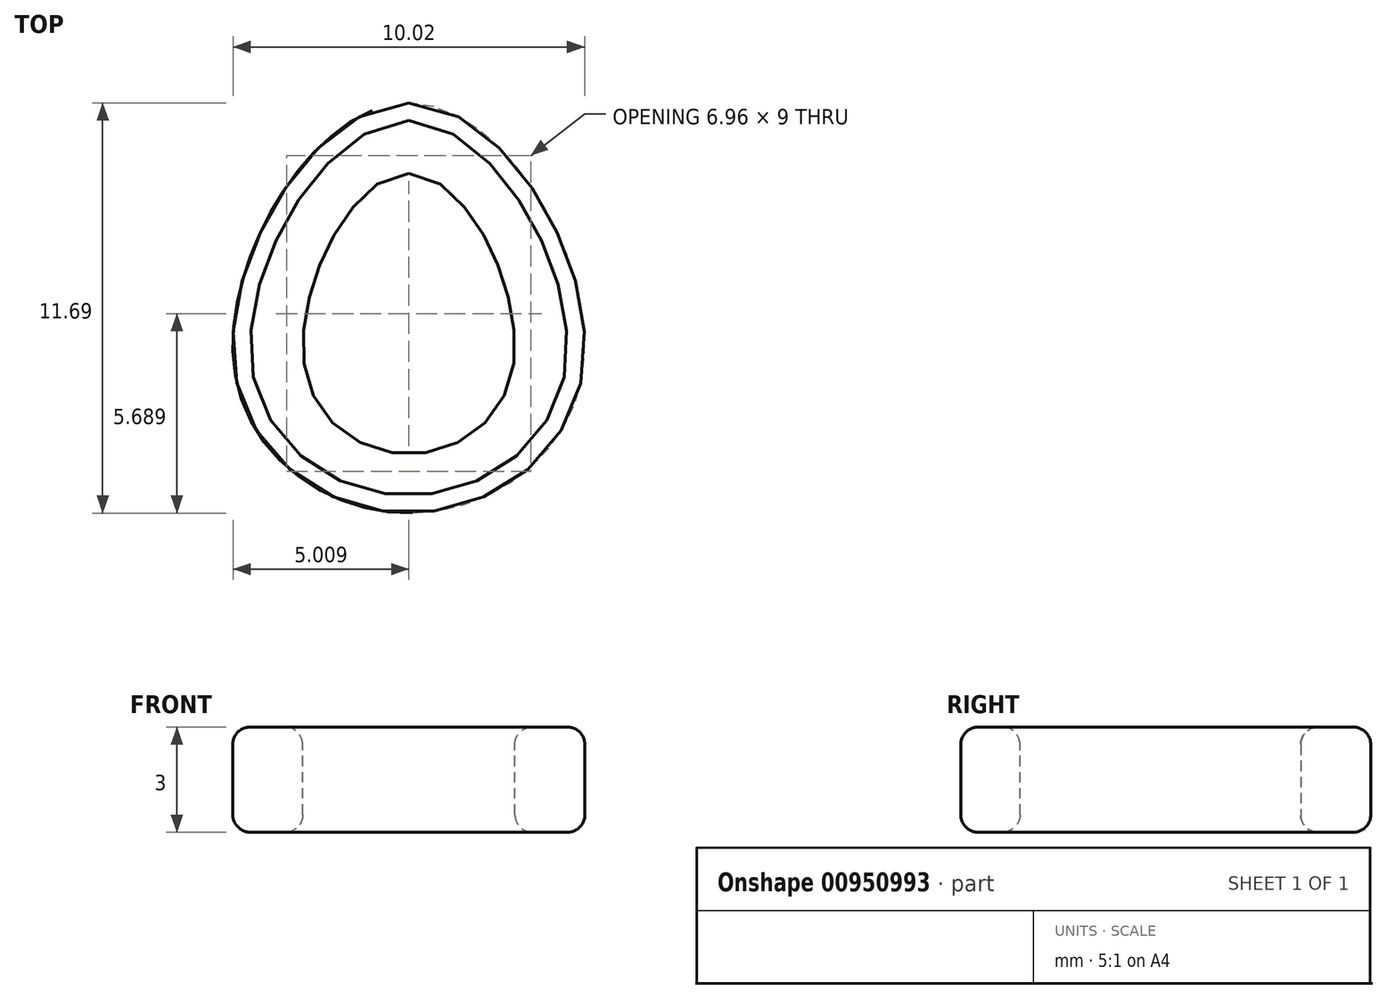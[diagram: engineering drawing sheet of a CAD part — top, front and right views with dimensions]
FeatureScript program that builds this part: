
annotation { "Feature Type Name" : "Feature", "Feature Type Description" : "" }
export const myFeature = defineFeature(function(context is Context, id is Id, definition is map)
    precondition{}
    {
        {
            var Q0;
            Q0=qCreatedBy(makeId("Top.planeOp"),FACE);
            var sketch = newSketch(context, id + "F0", { "sketchPlane" : qUnion([Q0])});
            skFitSpline(sketch, "E0", {"points": [v(0, 5.36) * mm, v(3, 0) * mm, v(0, -2.64) * mm, v(-3, 0) * mm, v(0, 5.36) * mm]});
            skFitSpline(sketch, "E1", {"points": [v(0, 7.36) * mm, v(5, 0) * mm, v(0, -4.33) * mm, v(-5, 0) * mm, v(0, 7.36) * mm]});
            skSolve(sketch);
        }
        {
            var Q0;
            Q0=makeQuery(id+"F0.imprint","IMPRINT",FACE,{"disambiguationData":[TD([[makeQuery(id+"F0.imprint","IMPRINT",EDGE,{"derivedFrom":sQuery(id+"F0.wireOp",EDGE,"E0")}),1.0]])]});
            extrude(context, id + "F1", {"entities" : qUnion([Q0]), "depth" : 3 * mm, "offsetDistance" : 25 * mm});
        }
        {
            var Q0;
            Q0=makeQuery(id+"F1.opExtrude","CAP_EDGE",EDGE,{"disambiguationData":[OSD([sQuery(id+"F0.wireOp",EDGE,"E1")])],"isStart":true});
            var Q1;
            Q1=makeQuery(id+"F1.opExtrude","CAP_EDGE",EDGE,{"disambiguationData":[OSD([sQuery(id+"F0.wireOp",EDGE,"E1")])],"isStart":false});
            var Q2;
            Q2=makeQuery(id+"F1.opExtrude","CAP_EDGE",EDGE,{"disambiguationData":[OSD([sQuery(id+"F0.wireOp",EDGE,"E0")])],"isStart":false});
            var Q3;
            Q3=makeQuery(id+"F1.opExtrude","CAP_EDGE",EDGE,{"disambiguationData":[OSD([sQuery(id+"F0.wireOp",EDGE,"E0")])],"isStart":true});
            fillet(context, id + "F2", {"entities" : qUnion([Q0, Q1, Q2, Q3]), "tangentPropagation" : true, "radius" : .5 * mm, "defaultsChanged" : true, "vertexSettings" : [], "allowEdgeOverflow" : false});
        }
    });
